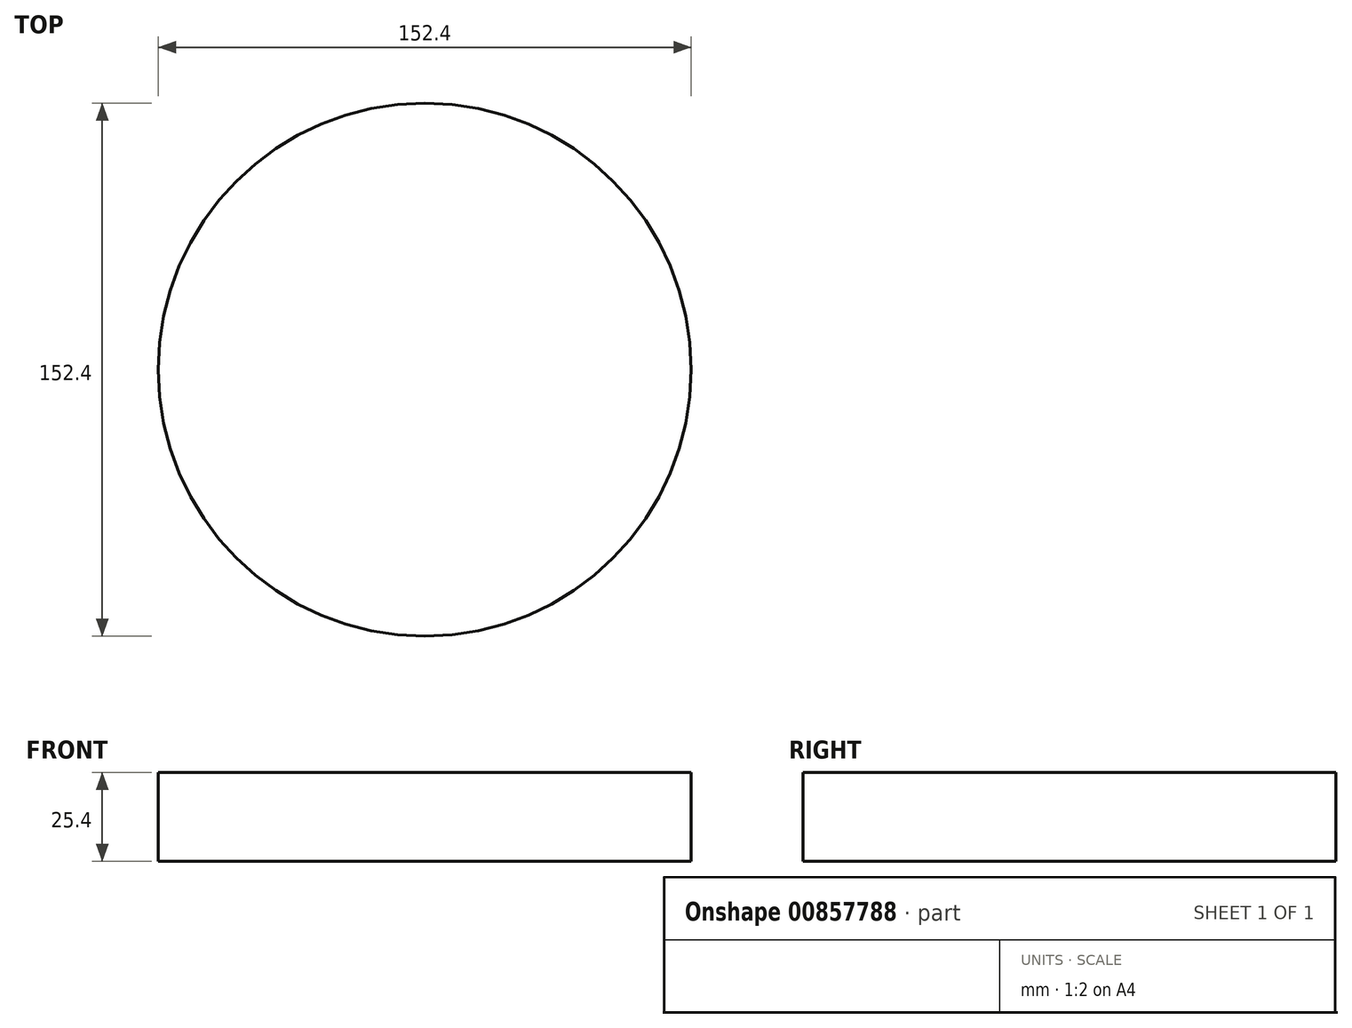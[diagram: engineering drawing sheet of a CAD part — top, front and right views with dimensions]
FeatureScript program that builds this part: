
annotation { "Feature Type Name" : "Feature", "Feature Type Description" : "" }
export const myFeature = defineFeature(function(context is Context, id is Id, definition is map)
    precondition{}
    {
        {
            var Q0;
            Q0=qCreatedBy(makeId("Top.planeOp"),FACE);
            var sketch = newSketch(context, id + "F0", { "sketchPlane" : qUnion([Q0])});
            skCircle(sketch, "E0", {"center": v(0, 0) * mm, "radius": 76.2 * mm});
            skSolve(sketch);
        }
        {
            var Q0;
            Q0 = qSketchRegion(id + "F0", true);
            extrude(context, id + "F1", {"entities" : qUnion([Q0]), "depth" : 25.4 * mm, "offsetDistance" : 25.4 * mm});
        }
    });
